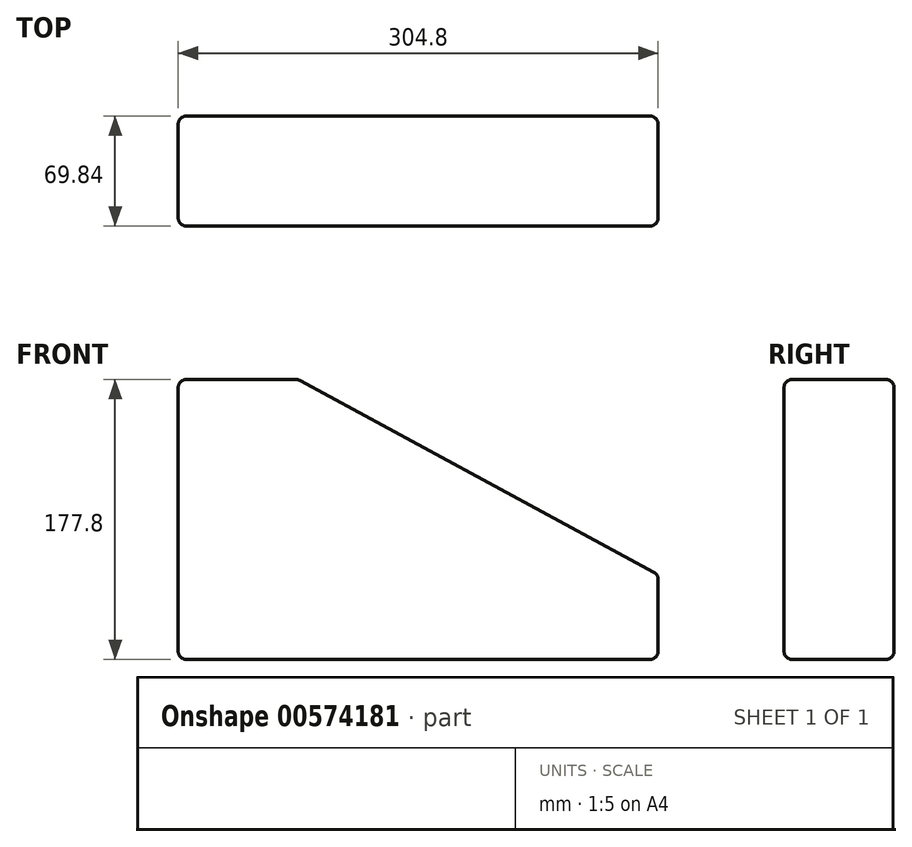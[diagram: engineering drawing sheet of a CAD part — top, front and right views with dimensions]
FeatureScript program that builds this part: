
annotation { "Feature Type Name" : "Feature", "Feature Type Description" : "" }
export const myFeature = defineFeature(function(context is Context, id is Id, definition is map)
    precondition{}
    {
        {
            var Q0;
            Q0=qCreatedBy(makeId("Front.planeOp"),FACE);
            var sketch = newSketch(context, id + "F0", { "sketchPlane" : qUnion([Q0])});
            skLineSegment(sketch, "E0", {"start": v(0, 0) * mm, "end": v(304.8, 0) * mm});
            skLineSegment(sketch, "E1", {"start": v(304.8, 0) * mm, "end": v(304.8, 53.98) * mm});
            skLineSegment(sketch, "E2", {"start": v(304.8, 53.97) * mm, "end": v(76.2, 177.8) * mm});
            skLineSegment(sketch, "E3", {"start": v(76.2, 177.8) * mm, "end": v(0, 177.8) * mm});
            skLineSegment(sketch, "E4", {"start": v(0, 177.8) * mm, "end": v(0, 0) * mm});
            skSolve(sketch);
        }
        {
            var Q0;
            Q0 = qSketchRegion(id + "F0", true);
            extrude(context, id + "F1", {"entities" : qUnion([Q0]), "depth" : 69.85 * mm, "offsetDistance" : 25.4 * mm, "symmetric" : true});
        }
        {
            var Q0;
            Q0=makeQuery(id+"F1.opExtrude","CAP_FACE",FACE,{"disambiguationData":[OSD([sQuery(id+"F0.wireOp",EDGE,"E0"),sQuery(id+"F0.wireOp",EDGE,"E1"),sQuery(id+"F0.wireOp",EDGE,"E2"),sQuery(id+"F0.wireOp",EDGE,"E3"),sQuery(id+"F0.wireOp",EDGE,"E4")])],"isStart":false});
            var Q1;
            Q1=makeQuery(id+"F1.opExtrude","CAP_FACE",FACE,{"disambiguationData":[OSD([sQuery(id+"F0.wireOp",EDGE,"E0"),sQuery(id+"F0.wireOp",EDGE,"E1"),sQuery(id+"F0.wireOp",EDGE,"E2"),sQuery(id+"F0.wireOp",EDGE,"E3"),sQuery(id+"F0.wireOp",EDGE,"E4")])],"isStart":true});
            var Q2;
            Q2=makeQuery(id+"F1.opExtrude","SWEPT_FACE",FACE,{"disambiguationData":[OSD([sQuery(id+"F0.wireOp",EDGE,"E3")])]});
            var Q3;
            Q3=makeQuery(id+"F1.opExtrude","SWEPT_FACE",FACE,{"disambiguationData":[OSD([sQuery(id+"F0.wireOp",EDGE,"E2")])]});
            var Q4;
            Q4=makeQuery(id+"F1.opExtrude","SWEPT_FACE",FACE,{"disambiguationData":[OSD([sQuery(id+"F0.wireOp",EDGE,"E0")])]});
            fillet(context, id + "F2", {"entities" : qUnion([Q0, Q1, Q2, Q3, Q4]), "radius" : 5.08 * mm, "tangentPropagation" : true, "allowEdgeOverflow" : false});
        }
    });
